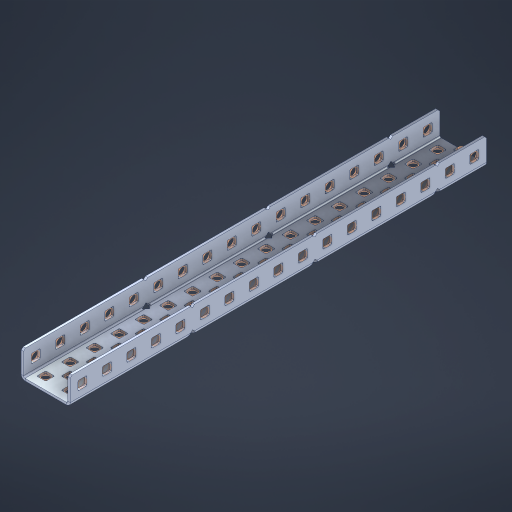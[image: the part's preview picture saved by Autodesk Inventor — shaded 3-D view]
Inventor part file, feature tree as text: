
AUTODESK INVENTOR PART (.ipt)
format: ipt  version: 2023 (Build 270158000, 158)  size: 1,257,472 bytes
history: native  units: in
note: dims shown in document units (in); Inventor stores cm internally (conversion verified against a paired STEP export)
features: other x92, extrude x83, sheet_metal_op x11, sketch x10, pattern_linear x2, mirror x1, chamfer x1
ambient origin geometry x8: Origin, YZ Plane, XZ Plane, XY Plane, X Axis, Y Axis, Z Axis, Center Point
bodies: Solid1 (feature_tree), Body (feature_tree)
feature tree (200):
  sheet_metal_op  "Flanges"
  other  "Flange Pattern Plane"
  other  "Flange Pattern Sketch"
  sheet_metal_op  "Flange Pattern"
  sheet_metal_op  "Body Pattern"
  pattern_linear  "Center Pattern"  Spacing1=0.0469in  [1 undecoded]
  other  "Arc Length"
  mirror  "Notch Mirror"
  pattern_linear  "Notch Pattern"  Spacing1=0.182in  [1 undecoded]
  chamfer  "End Chamfer"
  extrude  "Half Cut"  Depth=0.02in
  sketch  "Sketch1"  dims[d0=1.0in]
  other  "Plate1"
  sketch  "Sketch2"  dims[d1=8.5in]
  other  "Plate2"
  sheet_metal_op  "Bend1"
  sheet_metal_op  "Corner1"
  sketch  "Sketch3"  dims[d2=0.0469in]
  sketch  "Sketch7"  dims[d3=0.0469in]
  other  "Srf1"
  other  "Srf2"
  sketch  "Sketch8"  dims[d4=0.0234in]
  sketch  "Sketch9"  dims[d5=0.0938in]
  other  "Srf91"
  sheet_metal_op  "Body Pattern Sketch"
  other  "Srf92"
  sketch  "Sketch13"  dims[d6=0.0469in]
  sketch  "Sketch14"  dims[d7=0.5in d8=90.0deg d9=0.0312in]
  sketch  "Sketch15"  dims[d10=0.1875in]
  sketch  "Sketch16"  dims[d11=0.0469in d12=0.0469in d16=0.182in d17=0.02in d18=0.0469in d19=0.0in d20=0.25in d21=0.25in d38=6.6929in d40=0.5in d41=0.7874in d43=1.0in d46=0.172in d47=1.0in d48=0.0in d49=0.182in d50=0.02in d51=0.25in d52=0.25in d53=0.0469in d54=0.0in d55=0.172in d56=1.0in d57=0.0in d58=0.25in d60=6.6929in d62=0.5in d63=0.7874in d65=0.5in d85=0.1227in d86=0.1659in d88=0.04in d89=0.0469in d90=0.0in d91=0.04in d92=0.0491in d95=2.5in d96=0.04in d97=0.25in d98=45.0deg d99=0.25in d100=0.5in d101=0.0in d102=2.497in d106=0.182in d107=0.02in d108=0.5in d109=0.5in d110=0.0469in d111=0.0in d112=0.172in d113=0.5in d114=0.0in d117=0.5in d118=0.5in d119=0.5in]
  other  "Srf786"
  other  "Srf823"
  other  "Srf824"
  other  "Srf825"
  other  "Srf826"
  other  "Srf827"
  other  "Srf828"
  other  "Srf829"
  other  "Srf856"
  other  "Srf857"
  other  "Srf858"
  other  "Srf859"
  other  "Srf860"
  other  "Srf861"
  other  "Srf862"
  other  "Srf889"
  other  "Srf890"
  other  "Srf891"
  other  "Srf892"
  other  "Srf893"
  other  "Srf894"
  other  "Srf895"
  other  "Srf896"
  other  "Srf922"
  other  "Srf923"
  other  "Srf924"
  other  "Srf925"
  other  "Srf926"
  other  "Srf959"
  other  "Srf960"
  other  "Srf961"
  other  "Srf962"
  other  "Srf963"
  other  "Srf996"
  other  "Srf997"
  other  "Srf998"
  other  "Srf999"
  other  "Srf1000"
  other  "Srf1143"
  other  "Srf1144"
  other  "Srf1145"
  other  "Srf1146"
  other  "Srf1147"
  other  "Srf1148"
  other  "Srf1149"
  other  "Srf1150"
  other  "Srf1151"
  other  "Srf1152"
  other  "Srf1153"
  other  "Srf1154"
  other  "Srf1155"
  other  "Srf1156"
  other  "Srf1157"
  other  "Srf1158"
  other  "Srf1159"
  other  "Srf1160"
  other  "Srf1161"
  other  "Srf1162"
  other  "Srf1199"
  other  "Srf1200"
  other  "Srf1201"
  other  "Srf1202"
  other  "Srf1203"
  other  "Srf1204"
  other  "Srf1205"
  other  "Srf1206"
  other  "Srf1207"
  other  "Srf1208"
  other  "Srf1209"
  other  "Srf1210"
  other  "Srf1211"
  other  "Srf1212"
  other  "Srf1213"
  other  "Srf1214"
  other  "Srf1215"
  other  "Srf1216"
  other  "Srf1217"
  other  "Srf1218"
  other  "Srf1255"
  other  "Srf1256"
  other  "Srf1257"
  sheet_metal_op  "Flange Stamp"
  sheet_metal_op  "Flange Circle"
  sheet_metal_op  "Body Stamp"
  sheet_metal_op  "Body Circle"
  other  "Center Stamp"
  other  "Center Circle"
  sheet_metal_op  "Notch"
  extrude  "ExtrusionSrf2"  Depth=0.0469in
  extrude  "ExtrusionSrf92"  TaperAngle=0.0deg  [1 undecoded]
  extrude  "ExtrusionSrf823"  Depth=0.5in
  extrude  "ExtrusionSrf824"  Depth=0.5in
  extrude  "ExtrusionSrf825"  Depth=0.5in
  extrude  "ExtrusionSrf826"  Depth=0.5in
  extrude  "ExtrusionSrf827"  Depth=1.0in TaperAngle=0.0deg
  extrude  "ExtrusionSrf828"  Depth=0.5in
  extrude  "ExtrusionSrf829"  Depth=0.02in
  extrude  "ExtrusionSrf856"  Depth=0.5in
  extrude  "ExtrusionSrf857"  Depth=0.5in
  extrude  "ExtrusionSrf858"  Depth=0.0469in
  extrude  "ExtrusionSrf859"  TaperAngle=0.0deg  [1 undecoded]
  extrude  "ExtrusionSrf860"  Depth=0.5in
  extrude  "ExtrusionSrf861"  Depth=1.0in TaperAngle=0.0deg
  extrude  "ExtrusionSrf862"  Depth=0.5in
  extrude  "ExtrusionSrf889"  Depth=0.5in
  extrude  "ExtrusionSrf890"  Depth=0.5in
  extrude  "ExtrusionSrf891"  Depth=0.5in
  extrude  "ExtrusionSrf892"  Depth=0.5in
  extrude  "ExtrusionSrf893"  Depth=0.5in
  extrude  "ExtrusionSrf894"  Depth=0.0469in
  extrude  "ExtrusionSrf895"  TaperAngle=0.0deg  [1 undecoded]
  extrude  "ExtrusionSrf896"  Depth=0.5in
  extrude  "ExtrusionSrf922"  Depth=0.5in
  extrude  "ExtrusionSrf923"  Depth=2.5in
  extrude  "ExtrusionSrf924"  Depth=0.5in TaperAngle=45.0deg
  extrude  "ExtrusionSrf925"  Depth=0.5in
  extrude  "ExtrusionSrf926"  Depth=0.5in TaperAngle=0.0deg
  extrude  "ExtrusionSrf959"  Depth=0.5in
  extrude  "ExtrusionSrf960"  Depth=0.5in
  extrude  "ExtrusionSrf961"  Depth=0.02in
  extrude  "ExtrusionSrf962"  Depth=0.5in
  extrude  "ExtrusionSrf963"  Depth=0.5in
  extrude  "ExtrusionSrf996"  Depth=0.0469in
  extrude  "ExtrusionSrf997"  TaperAngle=0.0deg  [1 undecoded]
  extrude  "ExtrusionSrf998"  Depth=0.5in
  extrude  "ExtrusionSrf999"  Depth=0.5in TaperAngle=0.0deg
  extrude  "ExtrusionSrf1000"  Depth=0.5in
  extrude  "ExtrusionSrf1143"  Depth=0.5in
  extrude  "ExtrusionSrf1144"  Depth=0.5in
  extrude  "ExtrusionSrf1145"  [1 undecoded]
  extrude  "ExtrusionSrf1146"  [1 undecoded]
  extrude  "ExtrusionSrf1147"  [1 undecoded]
  extrude  "ExtrusionSrf1148"  [1 undecoded]
  extrude  "ExtrusionSrf1149"  [1 undecoded]
  extrude  "ExtrusionSrf1150"  [1 undecoded]
  extrude  "ExtrusionSrf1151"  [1 undecoded]
  extrude  "ExtrusionSrf1152"  [1 undecoded]
  extrude  "ExtrusionSrf1153"  [1 undecoded]
  extrude  "ExtrusionSrf1154"  [1 undecoded]
  extrude  "ExtrusionSrf1155"  [1 undecoded]
  extrude  "ExtrusionSrf1156"  [1 undecoded]
  extrude  "ExtrusionSrf1157"  [1 undecoded]
  extrude  "ExtrusionSrf1158"  [1 undecoded]
  extrude  "ExtrusionSrf1159"  [1 undecoded]
  extrude  "ExtrusionSrf1160"  [1 undecoded]
  extrude  "ExtrusionSrf1161"  [1 undecoded]
  extrude  "ExtrusionSrf1162"  [1 undecoded]
  extrude  "ExtrusionSrf1199"  [1 undecoded]
  extrude  "ExtrusionSrf1200"  [1 undecoded]
  extrude  "ExtrusionSrf1201"  [1 undecoded]
  extrude  "ExtrusionSrf1202"  [1 undecoded]
  extrude  "ExtrusionSrf1203"  [1 undecoded]
  extrude  "ExtrusionSrf1204"  [1 undecoded]
  extrude  "ExtrusionSrf1205"  [1 undecoded]
  extrude  "ExtrusionSrf1206"  [1 undecoded]
  extrude  "ExtrusionSrf1207"  [1 undecoded]
  extrude  "ExtrusionSrf1208"  [1 undecoded]
  extrude  "ExtrusionSrf1209"  [1 undecoded]
  extrude  "ExtrusionSrf1210"  [1 undecoded]
  extrude  "ExtrusionSrf1211"  [1 undecoded]
  extrude  "ExtrusionSrf1212"  [1 undecoded]
  extrude  "ExtrusionSrf1213"  [1 undecoded]
  extrude  "ExtrusionSrf1214"  [1 undecoded]
  extrude  "ExtrusionSrf1215"  [1 undecoded]
  extrude  "ExtrusionSrf1216"  [1 undecoded]
  extrude  "ExtrusionSrf1217"  [1 undecoded]
  extrude  "ExtrusionSrf1218"  [1 undecoded]
  extrude  "ExtrusionSrf1255"  [1 undecoded]
  extrude  "ExtrusionSrf1256"  [1 undecoded]
  extrude  "ExtrusionSrf1257"  [1 undecoded]
note: 47 required parameter values undecoded (feature->parameter linkage not recoverable at this tier; creation-order binding heuristic only, values carry confidence <= 0.55)
